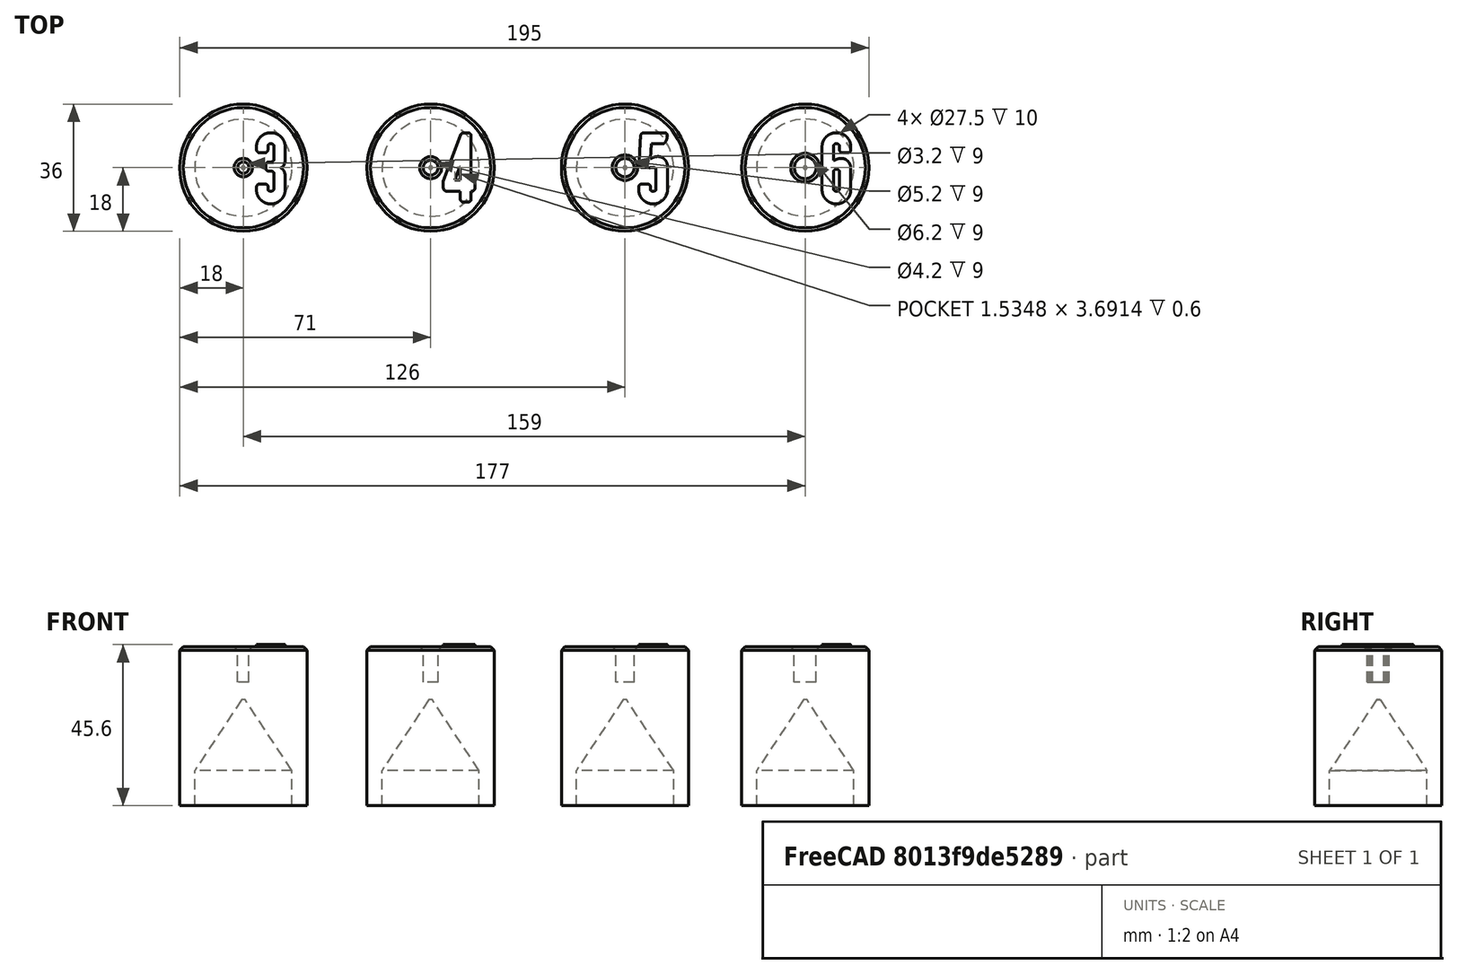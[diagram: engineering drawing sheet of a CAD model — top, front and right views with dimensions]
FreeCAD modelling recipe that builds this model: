
FCSTD DOCUMENT  (FreeCAD 0.19R24276 (Git))
Label: rod adapter
License: All rights reserved
LicenseURL: http://en.wikipedia.org/wiki/All_rights_reserved
objects: Part::Cylinder×6, Part::MultiFuse×5, Part::Cut×5, Part::Chamfer×4, Part::Part2DObjectPython×4, Part::Extrusion×4, Part::FeaturePython×2, Part::Cone×1
note: 31 computed .brp shape members not serialized (recipe doc carries the construction recipe); baked Part::Feature solids carry a one-line shape summary decoded from their .brp

FEATURE [Part::Cylinder] Cylinder
  Angle = 360
  AttacherType = Attacher::AttachEngine3D
  Height = 10
  Radius = 13.75
FEATURE [Part::Cone] Cone
  Angle = 360
  AttacherType = Attacher::AttachEngine3D
  Height = 20
  Placement = pos=(0,0,10) rot=(0,0,1;0rad)
  Radius1 = 13.75
  Radius2 = 0.5
FEATURE [Part::MultiFuse] Fusion
  Shapes = -> [Cone,Cylinder]
FEATURE [Part::Cylinder] Cylinder001
  Angle = 360
  AttacherType = Attacher::AttachEngine3D
  Height = 45
  Radius = 18
FEATURE [Part::Cut] Cut
  Base = -> Cylinder001
  Tool = -> Fusion
FEATURE [Part::FeaturePython] Clone  label="Cut001"  # Draft clone (typed FeaturePython)
  AttacherType = Attacher::AttachEngine3D
  Fuse = false
  Objects = -> [Cut]
  Scale = (1,1,1)
FEATURE [Part::FeaturePython] Clone001  label="Cut002"  # Draft clone (typed FeaturePython)
  AttacherType = Attacher::AttachEngine3D
  Fuse = false
  Objects = -> [Cut]
  Scale = (1,1,1)
FEATURE [Part::Cylinder] Cylinder002
  Angle = 360
  AttacherType = Attacher::AttachEngine3D
  Height = 10
  Placement = pos=(0,0,35) rot=(0,0,1;0rad)
  Radius = 1.6
FEATURE [Part::Cut] Cut001  label="Cut003"
  Base = -> Cut
  Tool = -> Cylinder002
FEATURE [Part::Chamfer] Chamfer
  Base = -> Cut001
  Edges = 2 edges r=1: [Edge1,Edge4]
FEATURE [Part::Part2DObjectPython] ShapeString  label="ShapeString 3"  # Draft 2D object (typed FeaturePython)
  FontFile = <path> Samuel-font-defharo.ttf
  Placement = pos=(3.13,-9.76,45) rot=(0,0,1;0rad)
  Size = 10
  String = 3
  Tracking = 0
FEATURE [Part::Extrusion] Extrude
  Base = -> ShapeString
  Dir = (0,0,1)
  DirMode = 2
  FaceMakerClass = Part::FaceMakerBullseye
  LengthFwd = 0.6
  LengthRev = 0
  Solid = false
  Symmetric = false
FEATURE [Part::MultiFuse] Fusion001  label="adapter 3mm"
  Placement = pos=(-53,0,0) rot=(0,0,1;0rad)
  Shapes = -> [Extrude,Chamfer]
FEATURE [Part::Part2DObjectPython] ShapeString001  label="ShapeString 4"  # Draft 2D object (typed FeaturePython)
  FontFile = <path> Samuel-font-defharo.ttf
  Placement = pos=(3.13,-9.76,45) rot=(0,0,1;0rad)
  Size = 10
  String = 4
  Tracking = 0
FEATURE [Part::Part2DObjectPython] ShapeString002  label="ShapeString 5"  # Draft 2D object (typed FeaturePython)
  FontFile = <path> Samuel-font-defharo.ttf
  Placement = pos=(3.13,-9.76,45) rot=(0,0,1;0rad)
  Size = 10
  String = 5
  Tracking = 0
FEATURE [Part::Extrusion] Extrude001
  Base = -> ShapeString001
  Dir = (0,0,1)
  DirMode = 2
  FaceMakerClass = Part::FaceMakerBullseye
  LengthFwd = 0.6
  LengthRev = 0
  Solid = false
  Symmetric = false
FEATURE [Part::Cylinder] Cylinder003
  Angle = 360
  AttacherType = Attacher::AttachEngine3D
  Height = 10
  Placement = pos=(0,0,35) rot=(0,0,1;0rad)
  Radius = 2.1
FEATURE [Part::Cut] Cut002  label="Cut004"
  Base = -> Clone
  Tool = -> Cylinder003
FEATURE [Part::Chamfer] Chamfer001
  Base = -> Cut002
  Edges = 2 edges r=1: [Edge1,Edge4]
FEATURE [Part::MultiFuse] Fusion002  label="adapter 4mm"
  Shapes = -> [Extrude001,Chamfer001]
FEATURE [Part::Extrusion] Extrude002
  Base = -> ShapeString002
  Dir = (0,0,1)
  DirMode = 2
  FaceMakerClass = Part::FaceMakerBullseye
  LengthFwd = 0.6
  LengthRev = 0
  Solid = false
  Symmetric = false
FEATURE [Part::Cylinder] Cylinder004
  Angle = 360
  AttacherType = Attacher::AttachEngine3D
  Height = 10
  Placement = pos=(0,0,35) rot=(0,0,1;0rad)
  Radius = 2.6
FEATURE [Part::Cut] Cut003  label="Cut005"
  Base = -> Clone001
  Tool = -> Cylinder004
FEATURE [Part::Chamfer] Chamfer002
  Base = -> Cut003
  Edges = 2 edges r=1: [Edge1,Edge4]
FEATURE [Part::MultiFuse] Fusion003  label="adapter 5mm"
  Placement = pos=(55,0,0) rot=(0,0,1;0rad)
  Shapes = -> [Extrude002,Chamfer002]
FEATURE [Part::Cylinder] Cylinder005
  Angle = 360
  AttacherType = Attacher::AttachEngine3D
  Height = 10
  Placement = pos=(0,0,35) rot=(0,0,1;0rad)
  Radius = 3.1
FEATURE [Part::Cut] Cut004  label="Cut006"
  Base = -> Clone001
  Tool = -> Cylinder005
FEATURE [Part::Chamfer] Chamfer003
  Base = -> Cut004
  Edges = 2 edges r=1: [Edge1,Edge4]
FEATURE [Part::Part2DObjectPython] ShapeString003  label="ShapeString 006"  # Draft 2D object (typed FeaturePython)
  FontFile = <path> Samuel-font-defharo.ttf
  Placement = pos=(4,-9.76,45) rot=(0,0,1;0rad)
  Size = 10
  String = 6
  Tracking = 0
FEATURE [Part::Extrusion] Extrude003
  Base = -> ShapeString003
  Dir = (0,0,1)
  DirMode = 2
  FaceMakerClass = Part::FaceMakerBullseye
  LengthFwd = 0.6
  LengthRev = 0
  Solid = false
  Symmetric = false
FEATURE [Part::MultiFuse] Fusion004  label="adapter 6"
  Placement = pos=(106,0,0) rot=(0,0,1;0rad)
  Shapes = -> [Extrude003,Chamfer003]
note: 4 file-system paths scrubbed to <path> (originals preserved in the JSON sidecar)
